# Revit family: Mailboxes_4C-Salsbury_Industries-Surface_Mounted-15_Door_High_Units
name_source: partatom
category: Specialty Equipment
revit_build: Autodesk Revit 2016 (Build: 20150714_1515(x64)
units: mm (PartAtom-declared; Revit-internal decimal feet)

## family parameters
Always vertical = Yes
Cut with Voids When Loaded = No
OmniClass Number = 23.40.90.14.11
OmniClass Title = Mail Boxes
Part Type = Normal
Room Calculation Point = No
Round Connector Dimension = Use Diameter
Shared = No
Work Plane-Based = No

## types (20) — shared parameters
4C Unit Elevation = 13.683 "
4C Unit Height = 55 "
Above Finished Floor (Bottom of Unit) = 13.12 "
Assembly Code = C1030910
Assembly Description = Mailboxes
Depth = 17.5 "
Height = 56.094 "
Lock Material = Stainless Steel - Salsbury Finish -  Polished
Manufacturer = Salsbury Industries
MasterFormat Number = 10 55 00
MasterFormat Title = Postal Specialties
OmniClass 23 Number = 23.40.90.14.11
OmniClass 23 Title = Mail Boxes
Type Comments = Surface Mounted 4C Horizontal Mailboxes - Front Loading
URL = www.mailboxes.com
Version = 1.0 (06/30/17)

## per-type parameters (varying)
| type | 4C Unit | Description | Width |
| 3815D-20 | Mailboxes_4C-Salsbury_Industries-Front_Load-15_Door_High_Units : 3715D-20 FL | 15 Door High Unit:  20 MB1, 2 PL4, OM2 | 32.25 " |
| 3815S-09 | Mailboxes_4C-Salsbury_Industries-Front_Load-15_Door_High_Units : 3715S-09 FL | 15 Door High Unit:  9 MB1, 1 PL4, OM2 | 17.496 " |
| 3815D-19 | Mailboxes_4C-Salsbury_Industries-Front_Load-15_Door_High_Units : 3715D-19 FL | 15 Door High Unit:  19 MB1, 1 PL4, 1 PL5, OM2 | 32.25 " |
| 3815D-18 | Mailboxes_4C-Salsbury_Industries-Front_Load-15_Door_High_Units : 3715D-18 FL | 15 Door High Unit:  18 MB1, 2 PL5, OM2 | 32.25 " |
| 3815D-17 | Mailboxes_4C-Salsbury_Industries-Front_Load-15_Door_High_Units : 3715D-17 FL | 15 Door High Unit:  17 MB1, 1 PL5, 1 PL6, OM2 | 32.25 " |
| 3815D-16 | Mailboxes_4C-Salsbury_Industries-Front_Load-15_Door_High_Units : 3715D-16 FL | 15 Door High Unit:  16 MB1, 2 PL6, OM2 | 32.25 " |
| 3815D-15 | Mailboxes_4C-Salsbury_Industries-Front_Load-15_Door_High_Units : 3715D-15 FL | 15 Door High Unit:  15 MB1, 2 PL6, OM3 | 32.25 " |
| 3815D-09 | Mailboxes_4C-Salsbury_Industries-Front_Load-15_Door_High_Units : 3715D-09 FL | 15 Door High Unit:  9 MB2, 2 PL5, OM2 | 32.25 " |
| 3815S-08 | Mailboxes_4C-Salsbury_Industries-Front_Load-15_Door_High_Units : 3715S-08 FL | 15 Door High Unit:  8 MB1, 1 PL5, OM2 | 17.496 " |
| 3815S-07 | Mailboxes_4C-Salsbury_Industries-Front_Load-15_Door_High_Units : 3715S-07 FL | 15 Door High Unit:  7 MB1, 1 PL6, OM2 | 17.496 " |
| 3815S-06 | Mailboxes_4C-Salsbury_Industries-Front_Load-15_Door_High_Units : 3715S-06 FL | 15 Door High Unit:  6 MB1, 1 PL6, OM3 | 17.496 " |
| 3815S-04 | Mailboxes_4C-Salsbury_Industries-Front_Load-15_Door_High_Units : 3715S-04 FL | 15 Door High Unit:  4 MB2, 1 PL5, OM2 | 17.496 " |
| 3815S-3P | Mailboxes_4C-Salsbury_Industries-Front_Load-15_Door_High_Units : 3715S-3P FL | 15 Door High Unit:  3 PL5 | 17.496 " |
| 3815D-29 | Mailboxes_4C-Salsbury_Industries-Front_Load-15_Door_High_Units : 3715D-29 FL | 15 Door High Unit:  29 MB1, CA | 32.25 " |
| 3815D-28 | Mailboxes_4C-Salsbury_Industries-Front_Load-15_Door_High_Units : 3715D-28 FL | 15 Door High Unit:  28 MB1, OM2 | 32.25 " |
| 3815D-13 | Mailboxes_4C-Salsbury_Industries-Front_Load-15_Door_High_Units : 3715D-13 FL | 15 Door High Unit:  11 MB2, 2 ,MB3, OM2 | 32.25 " |
| 3815S-14 | Mailboxes_4C-Salsbury_Industries-Front_Load-15_Door_High_Units : 3715S-14 FL | 15 Door High Unit:  14 MB1, CA | 17.496 " |
| 3815S-13 | Mailboxes_4C-Salsbury_Industries-Front_Load-15_Door_High_Units : 3715S-13 FL | 15 Door High Unit:  13 MB1, OM2 | 17.496 " |
| 3815S-2B | Mailboxes_4C-Salsbury_Industries-Front_Load-15_Door_High_Units : 3715S-2B FL | 15 Door High Unit:  2 Receptacle Bins | 17.496 " |
| 3815S-1C | Mailboxes_4C-Salsbury_Industries-Front_Load-15_Door_High_Units : 3715S-1C FL | 15 Door High Unit:  1 Collection Box | 17.496 " |

note: column(s) folded — value = type name in every type: Model

## geometry (parser evidence)
native form markers: Blend x6, Extrusion x1, Sweep x25
no freeform markers — native parametric forms only
